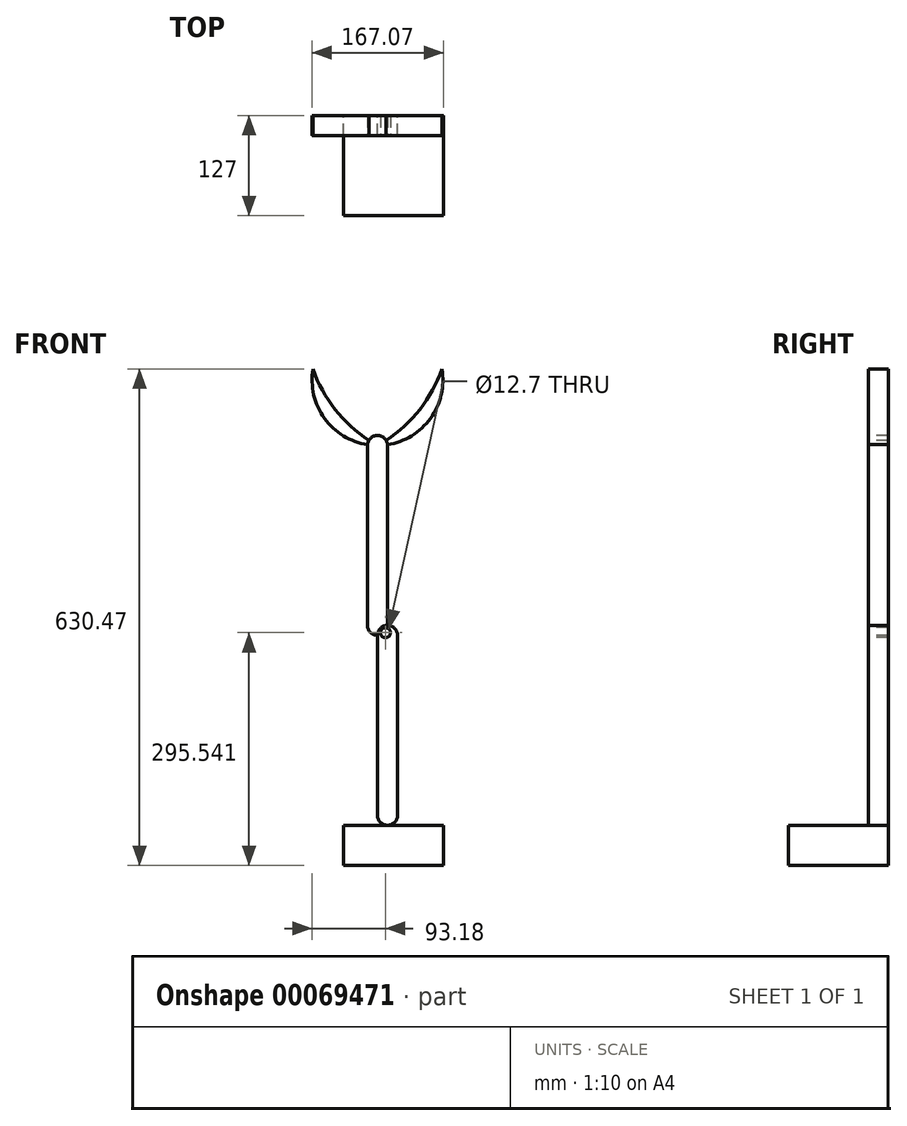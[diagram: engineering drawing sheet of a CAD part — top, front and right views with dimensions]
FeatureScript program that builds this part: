
annotation { "Feature Type Name" : "Feature", "Feature Type Description" : "" }
export const myFeature = defineFeature(function(context is Context, id is Id, definition is map)
    precondition{}
    {
        {
            var Q0;
            Q0=qCreatedBy(makeId("Front.planeOp"),FACE);
            var sketch = newSketch(context, id + "F0", { "sketchPlane" : qUnion([Q0])});
            skLineSegment(sketch, "E0.bottom", {"start": v(-61.76, -36.43) * mm, "end": v(65.24, -36.43) * mm});
            skLineSegment(sketch, "E0.top", {"start": v(-61.76, -87.23) * mm, "end": v(65.24, -87.23) * mm});
            skLineSegment(sketch, "E0.left", {"start": v(-61.76, -36.43) * mm, "end": v(-61.76, -87.23) * mm});
            skLineSegment(sketch, "E0.right", {"start": v(65.24, -36.43) * mm, "end": v(65.24, -87.23) * mm});
            skSolve(sketch);
        }
        {
            var Q0;
            Q0=makeQuery(id+"F0.imprint","IMPRINT",FACE,{"disambiguationData":[TD([[makeQuery(id+"F0.imprint","IMPRINT",EDGE,{"derivedFrom":sQuery(id+"F0.wireOp",EDGE,"E0.bottom")}),-1.0]])]});
            extrude(context, id + "F1", {"entities" : qUnion([Q0]), "depth" : 127 * mm});
        }
        {
            var Q0;
            Q0=qCreatedBy(makeId("Front.planeOp"),FACE);
            var sketch = newSketch(context, id + "F2", { "sketchPlane" : qUnion([Q0])});
            skLineSegment(sketch, "E1.bottom", {"start": v(-6.05, -36.43) * mm, "end": v(-6.05, -36.43) * mm});
            skLineSegment(sketch, "E1.top", {"start": v(-6.05, 217.57) * mm, "end": v(-6.05, 217.57) * mm});
            skLineSegment(sketch, "E1.left", {"start": v(-18.75, -23.73) * mm, "end": v(-18.75, 204.87) * mm});
            skLineSegment(sketch, "E1.right", {"start": v(6.65, -23.73) * mm, "end": v(6.65, 204.87) * mm});
            skPoint(sketch, "E2.visualSharp", {"position": v(-18.75, -36.43) * mm});
            skArc(sketch, "E2.filletArc", {"start": v(-18.75, -23.73) * mm, "mid": v(-15.03, -32.7) * mm, "end": v(-6.05, -36.43) * mm});
            skPoint(sketch, "E3.visualSharp", {"position": v(6.65, -36.43) * mm});
            skArc(sketch, "E3.filletArc", {"start": v(-6.05, -36.43) * mm, "mid": v(2.93, -32.7) * mm, "end": v(6.65, -23.73) * mm});
            skPoint(sketch, "E4.visualSharp", {"position": v(-18.75, 217.57) * mm});
            skArc(sketch, "E4.filletArc", {"start": v(-6.05, 217.57) * mm, "mid": v(-15.03, 213.85) * mm, "end": v(-18.75, 204.87) * mm});
            skPoint(sketch, "E5.visualSharp", {"position": v(6.65, 217.57) * mm});
            skArc(sketch, "E5.filletArc", {"start": v(6.65, 204.87) * mm, "mid": v(2.93, 213.85) * mm, "end": v(-6.05, 217.57) * mm});
            skSolve(sketch);
        }
        {
            var Q0;
            Q0=makeQuery(id+"F2.imprint","IMPRINT",FACE,{"disambiguationData":[TD([[makeQuery(id+"F2.imprint","IMPRINT",EDGE,{"derivedFrom":sQuery(id+"F2.wireOp",EDGE,"E1.left")}),-1.0]])]});
            extrude(context, id + "F3", {"entities" : qUnion([Q0]), "operationType" : NewBodyOperationType.ADD, "depth" : 25.4 * mm});
        }
        {
            var Q0;
            Q0=makeQuery(id+"F3.opExtrude","CAP_FACE",FACE,{"disambiguationData":[OSD([sQuery(id+"F2.wireOp",EDGE,"E1.left"),sQuery(id+"F2.wireOp",EDGE,"E1.right"),sQuery(id+"F2.wireOp",EDGE,"E2.filletArc"),sQuery(id+"F2.wireOp",EDGE,"E3.filletArc"),sQuery(id+"F2.wireOp",EDGE,"E4.filletArc"),sQuery(id+"F2.wireOp",EDGE,"E5.filletArc")])],"isStart":false});
            var sketch = newSketch(context, id + "F4", { "sketchPlane" : qUnion([Q0])});
            skLineSegment(sketch, "E6.bottom", {"start": v(-18.75, 204.87) * mm, "end": v(-18.75, 204.87) * mm});
            skLineSegment(sketch, "E6.top", {"start": v(-18.75, 458.87) * mm, "end": v(-18.75, 458.87) * mm});
            skLineSegment(sketch, "E6.left", {"start": v(-6.05, 217.57) * mm, "end": v(-6.05, 446.17) * mm});
            skLineSegment(sketch, "E6.right", {"start": v(-31.45, 217.57) * mm, "end": v(-31.45, 446.17) * mm});
            skPoint(sketch, "E7.visualSharp", {"position": v(-31.45, 204.87) * mm});
            skArc(sketch, "E7.filletArc", {"start": v(-31.45, 217.57) * mm, "mid": v(-27.73, 208.6) * mm, "end": v(-18.75, 204.87) * mm});
            skPoint(sketch, "E8.visualSharp", {"position": v(-6.05, 204.87) * mm});
            skArc(sketch, "E8.filletArc", {"start": v(-18.75, 204.87) * mm, "mid": v(-9.77, 208.6) * mm, "end": v(-6.05, 217.57) * mm});
            skPoint(sketch, "E9.visualSharp", {"position": v(-31.45, 458.87) * mm});
            skArc(sketch, "E9.filletArc", {"start": v(-18.75, 458.87) * mm, "mid": v(-27.73, 455.15) * mm, "end": v(-31.45, 446.17) * mm});
            skPoint(sketch, "E10.visualSharp", {"position": v(-6.05, 458.87) * mm});
            skArc(sketch, "E10.filletArc", {"start": v(-6.05, 446.17) * mm, "mid": v(-9.77, 455.15) * mm, "end": v(-18.75, 458.87) * mm});
            skSolve(sketch);
        }
        {
            var Q0;
            Q0=makeQuery(id+"F4.imprint","IMPRINT",FACE,{"disambiguationData":[TD([[makeQuery(id+"F4.imprint","IMPRINT",EDGE,{"derivedFrom":sQuery(id+"F4.wireOp",EDGE,"E6.top")}),1.0]])]});
            var Q1;
            {var subQ1=sQuery(id+"F4.wireOp",EDGE,"E6.left");Q1=makeQuery(id+"F4.imprint","IMPRINT",FACE,{"disambiguationData":[TD([[makeQuery(id+"F4.imprint","IMPRINT",EDGE,{"derivedFrom":subQ1}),1.0]])]});}
            extrude(context, id + "F5", {"entities" : qUnion([Q0, Q1]), "oppositeDirection" : true, "depth" : 25.4 * mm});
        }
        {
            var Q0;
            Q0=makeQuery(id+"F5.opExtrude","CAP_FACE",FACE,{"disambiguationData":[OSD([sQuery(id+"F2.wireOp",EDGE,"E4.filletArc"),sQuery(id+"F2.wireOp",EDGE,"E5.filletArc"),sQuery(id+"F4.wireOp",EDGE,"E6.left"),sQuery(id+"F4.wireOp",EDGE,"E6.right"),sQuery(id+"F4.wireOp",EDGE,"E7.filletArc"),sQuery(id+"F4.wireOp",EDGE,"E9.filletArc"),sQuery(id+"F4.wireOp",EDGE,"E10.filletArc")])],"isStart":true});
            var sketch = newSketch(context, id + "F6", { "sketchPlane" : qUnion([Q0])});
            skArc(sketch, "E11", {"start": v(-100.64, 543.24) * mm, "mid": v(-82.25, 475.68) * mm, "end": v(-18.75, 446.17) * mm});
            skArc(sketch, "E12", {"start": v(-100.64, 543.24) * mm, "mid": v(-68.66, 487.14) * mm, "end": v(-18.75, 446.17) * mm});
            skArc(sketch, "E13", {"start": v(-18.75, 446.17) * mm, "mid": v(44.75, 475.68) * mm, "end": v(63.15, 543.24) * mm});
            skArc(sketch, "E14", {"start": v(-18.75, 446.17) * mm, "mid": v(31.16, 487.14) * mm, "end": v(63.15, 543.24) * mm});
            skSolve(sketch);
        }
        {
            var Q0;
            {var subQ0=sQuery(id+"F6.wireOp",EDGE,"E12");var subQ1=sQuery(id+"F6.wireOp",EDGE,"E11");var subQ2=makeQuery(id+"F6.imprint","INTERSECT",VERTEX,{"derivedFrom":[subQ1,subQ0]});Q0=makeQuery(id+"F6.imprint","IMPRINT",FACE,{"disambiguationData":[TD([[makeQuery(id+"F6.imprint","IMPRINT",EDGE,{"disambiguationData":[TD([[subQ2,-1.0]])],"derivedFrom":subQ1}),1.0]])]});}
            var Q1;
            {var subQ0=sQuery(id+"F6.wireOp",EDGE,"E14");var subQ1=sQuery(id+"F6.wireOp",EDGE,"E13");var subQ2=makeQuery(id+"F6.imprint","INTERSECT",VERTEX,{"derivedFrom":[subQ1,subQ0]});Q1=makeQuery(id+"F6.imprint","IMPRINT",FACE,{"disambiguationData":[TD([[makeQuery(id+"F6.imprint","IMPRINT",EDGE,{"disambiguationData":[TD([[subQ2,1.0]])],"derivedFrom":subQ1}),1.0]])]});}
            extrude(context, id + "F7", {"entities" : qUnion([Q0, Q1]), "oppositeDirection" : true, "depth" : 25.4 * mm});
        }
        {
            var Q0;
            Q0=makeQuery(id+"F3.opExtrude","CAP_FACE",FACE,{"disambiguationData":[OSD([sQuery(id+"F2.wireOp",EDGE,"E1.left"),sQuery(id+"F2.wireOp",EDGE,"E1.right"),sQuery(id+"F2.wireOp",EDGE,"E2.filletArc"),sQuery(id+"F2.wireOp",EDGE,"E3.filletArc"),sQuery(id+"F2.wireOp",EDGE,"E4.filletArc"),sQuery(id+"F2.wireOp",EDGE,"E5.filletArc")])],"isStart":false});
            var sketch = newSketch(context, id + "F8", { "sketchPlane" : qUnion([Q0])});
            skCircle(sketch, "E15", {"center": v(-8.65, 208.31) * mm, "radius": 6.35 * mm});
            skSolve(sketch);
        }
        {
            var Q0;
            Q0=makeQuery(id+"F8.imprint","IMPRINT",FACE,{"disambiguationData":[TD([[makeQuery(id+"F8.imprint","IMPRINT",EDGE,{"derivedFrom":sQuery(id+"F8.wireOp",EDGE,"E15")}),1.0]])]});
            extrude(context, id + "F9", {"entities" : qUnion([Q0]), "operationType" : NewBodyOperationType.REMOVE, "endBound" : BoundingType.THROUGH_ALL, "oppositeDirection" : true, "depth" : 25.4 * mm});
        }
    });
